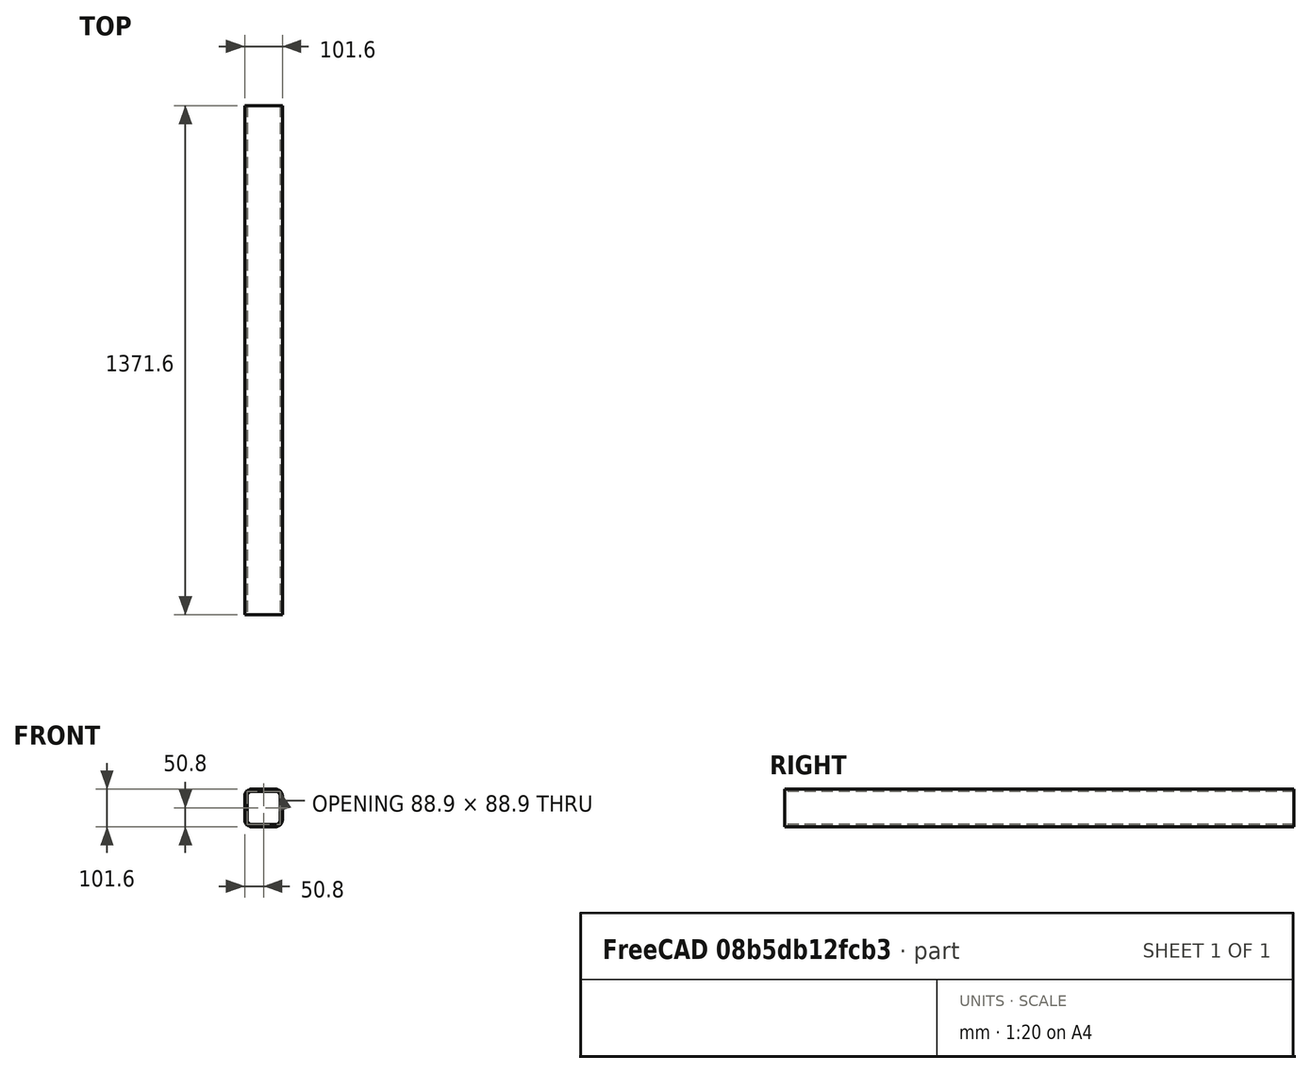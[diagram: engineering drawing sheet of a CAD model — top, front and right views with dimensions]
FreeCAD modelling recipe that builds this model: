
FCSTD DOCUMENT  (FreeCAD 0.18R16131 (Git))
Label: YAxisAssembly
License: All rights reserved
LicenseURL: http://en.wikipedia.org/wiki/All_rights_reserved
objects: Mesh::Feature×8, Sketcher::SketchObject×4, PartDesign::Pad×3, PartDesign::Fillet×2, App::Part×2, Spreadsheet::Sheet×1, PartDesign::Pocket×1, PartDesign::Body×1
note: 15 computed .brp shape members not serialized (recipe doc carries the construction recipe); baked Part::Feature solids carry a one-line shape summary decoded from their .brp

FEATURE [Spreadsheet::Sheet] Spreadsheet  label="p"
  cells = A1=Title; B1=Desired Dimension; C1=Converted to mm; A2=Width; B2=4; C2(w)==B2 * 25.4; A3=Length; B3==4 * 12 + 6; C3(length)==B3 * 25.4; A4=Wall Thickness; B4==1 / 4; C4(th)==B4 * 25.4; A5=Tolerance; C5(tol)=2; A6=BevelEdge; B6=0.75; C6(bevel)==B6 * 25.4
FEATURE [Sketcher::SketchObject] Sketch  label="4x4BodySketch"
  MapMode = 5
  Placement = pos=(0,0,0) rot=(0.57735,0.57735,0.57735;2.0944rad)
  Support = -> [YZ_Plane]
  expr: Constraints[6] = p.w
  sketch-geometry (4):
    g0: LineSegment StartX=-50.8 StartY=50.8 StartZ=0 EndX=50.8 EndY=50.8 EndZ=0
    g1: LineSegment StartX=50.8 StartY=50.8 StartZ=0 EndX=50.8 EndY=-50.8 EndZ=0
    g2: LineSegment StartX=50.8 StartY=-50.8 StartZ=0 EndX=-50.8 EndY=-50.8 EndZ=0
    g3: LineSegment StartX=-50.8 StartY=-50.8 StartZ=0 EndX=-50.8 EndY=50.8 EndZ=0
  constraints (10):
    c: Coincident(g0,g1)
    c: Coincident(g1,g2)
    c: Coincident(g2,g3)
    c: Coincident(g3,g0)
    c: Horizontal(g2)
    c: Vertical(g1)
    c: DistanceX(g0,g0) = 101.6
    c: Equal(g1,g0)
    c: Symmetric(g0,g0,g-2)
    c: Symmetric(g0,g2,g-1)
FEATURE [PartDesign::Pad] Pad  label="4x4Pad"
  Length = 1371.6
  Length2 = 100.076
  Placement = pos=(0,0,0) rot=(0.57735,0.57735,0.57735;2.0944rad)
  Profile = -> Sketch
  Type = 0
  expr: Length = p.length
FEATURE [PartDesign::Fillet] Fillet  label="OuterBevel"
  Base = -> Pad [Edge2,Edge1,Edge5,Edge8]
  BaseFeature = -> Pad
  Placement = pos=(0,0,0) rot=(0.57735,0.57735,0.57735;2.0944rad)
  Radius = 19.05
  expr: Radius = p.bevel
FEATURE [Sketcher::SketchObject] Sketch001  label="4x4HoleSketch"
  MapMode = 5
  Placement = pos=(0,0,0) rot=(0.57735,0.57735,0.57735;2.0944rad)
  Support = -> [YZ_Plane]
  expr: Constraints[7] = p.w - p.th * 2
  sketch-geometry (4):
    g0: LineSegment StartX=-44.45 StartY=44.45 StartZ=0 EndX=44.45 EndY=44.45 EndZ=0
    g1: LineSegment StartX=44.45 StartY=44.45 StartZ=0 EndX=44.45 EndY=-44.45 EndZ=0
    g2: LineSegment StartX=44.45 StartY=-44.45 StartZ=0 EndX=-44.45 EndY=-44.45 EndZ=0
    g3: LineSegment StartX=-44.45 StartY=-44.45 StartZ=0 EndX=-44.45 EndY=44.45 EndZ=0
  constraints (10):
    c: Coincident(g0,g1)
    c: Coincident(g1,g2)
    c: Coincident(g2,g3)
    c: Coincident(g3,g0)
    c: Horizontal(g2)
    c: Vertical(g3)
    c: Equal(g1,g0)
    c: DistanceX(g0,g0) = 88.9
    c: Symmetric(g0,g0,g-2)
    c: Symmetric(g1,g0,g-1)
FEATURE [PartDesign::Pocket] Pocket  label="4x4HolePocket"
  BaseFeature = -> Fillet
  Length = 5.08
  Length2 = 100.076
  Placement = pos=(0,0,0) rot=(0.57735,0.57735,0.57735;2.0944rad)
  Profile = -> Sketch001
  Reversed = true
  Type = 1
FEATURE [PartDesign::Fillet] Fillet001  label="InnerBevel"
  Base = -> Pocket [Edge36,Edge34,Edge33,Edge35]
  BaseFeature = -> Pocket
  Placement = pos=(0,0,0) rot=(0.57735,0.57735,0.57735;2.0944rad)
  Radius = 12.7
  expr: Radius = p.bevel - p.th
FEATURE [PartDesign::Body] Body  label="4x4Tube"
  Group = -> [Sketch,Pad,Fillet,Sketch001,Pocket,Fillet001]
  Origin = -> Origin
  Placement = pos=(0,0,0) rot=(0.57735,-0.57735,0.57735;4.18879rad)
  Tip = -> Fillet001
FEATURE [Mesh::Feature] EndPlug
  Placement = pos=(0,0,0) rot=(0,0,1;4.71239rad)
FEATURE [Mesh::Feature] EndPlug001
  Placement = pos=(-9.3e-15,-1372,0) rot=(0.707107,0.707107,0;3.14159rad)
FEATURE [Sketcher::SketchObject] Sketch002
  MapMode = 5
  Placement = pos=(0,0,0) rot=(0.57735,0.57735,0.57735;2.0944rad)
  sketch-geometry (1):
    g0: Circle CenterX=-63.0911 CenterY=-108.926 CenterZ=0 NormalX=0 NormalY=0 NormalZ=1 AngleXU=0 Radius=12.7
  constraints (1):
    c: Radius(g0) = 12.7
FEATURE [PartDesign::Pad] Pad001  label="1inShaft"
  Length = 1527.05
  Length2 = 100.08
  Placement = pos=(0,0,0) rot=(0.57735,0.57735,0.57735;2.0944rad)
  Profile = -> Sketch002
  Reversed = true
  Type = 0
FEATURE [App::Part] Part  label="1inShaft001"
  Group = -> [Sketch002,Pad001]
  Origin = -> Origin001
  Placement = pos=(39,77,60) rot=(0,0,1;1.5708rad)
FEATURE [Sketcher::SketchObject] Sketch003
  MapMode = 5
  Placement = pos=(0,0,0) rot=(0.57735,0.57735,0.57735;2.0944rad)
  sketch-geometry (1):
    g0: Circle CenterX=-63.0911 CenterY=-108.926 CenterZ=0 NormalX=0 NormalY=0 NormalZ=1 AngleXU=0 Radius=12.7
  constraints (1):
    c: Radius(g0) = 12.7
FEATURE [PartDesign::Pad] Pad002  label="1inShaft003"
  Length = 1527.05
  Length2 = 100.08
  Placement = pos=(0,0,0) rot=(0.57735,0.57735,0.57735;2.0944rad)
  Profile = -> Sketch003
  Reversed = true
  Type = 0
FEATURE [App::Part] Part001  label="1inShaft002"
  Group = -> [Sketch003,Pad002]
  Origin = -> Origin002
  Placement = pos=(39.5,77,157.1) rot=(0,0,1;1.5708rad)
FEATURE [Mesh::Feature] Cnc_torch_idler_v19_012
  Placement = pos=(112.4,-1472.2,-9.726e-13) rot=(0,-0.707107,-0.707107;3.14159rad)
FEATURE [Mesh::Feature] Cnc_torch_idler_v19_011
  Placement = pos=(91,-1472.3,-9.707e-13) rot=(-1,0,0;1.5708rad)
FEATURE [Mesh::Feature] CNC_Torch_1708_motorside
  Placement = pos=(43.5,136.2,-3.2e-14) rot=(-1,0,0;1.5708rad)
FEATURE [Mesh::Feature] CNC_Torch_1708_motorside001
  Placement = pos=(160.7,136.2,-3.2e-14) rot=(0,-0.707107,-0.707107;3.14159rad)
FEATURE [Mesh::Feature] carriage
  Placement = pos=(102,-1300,-3.053e-13) rot=(0.57735,0.57735,0.57735;2.0944rad)
FEATURE [Mesh::Feature] carriage001
  Placement = pos=(102,-1300,-3.053e-13) rot=(-0.57735,0.57735,0.57735;4.18879rad)
